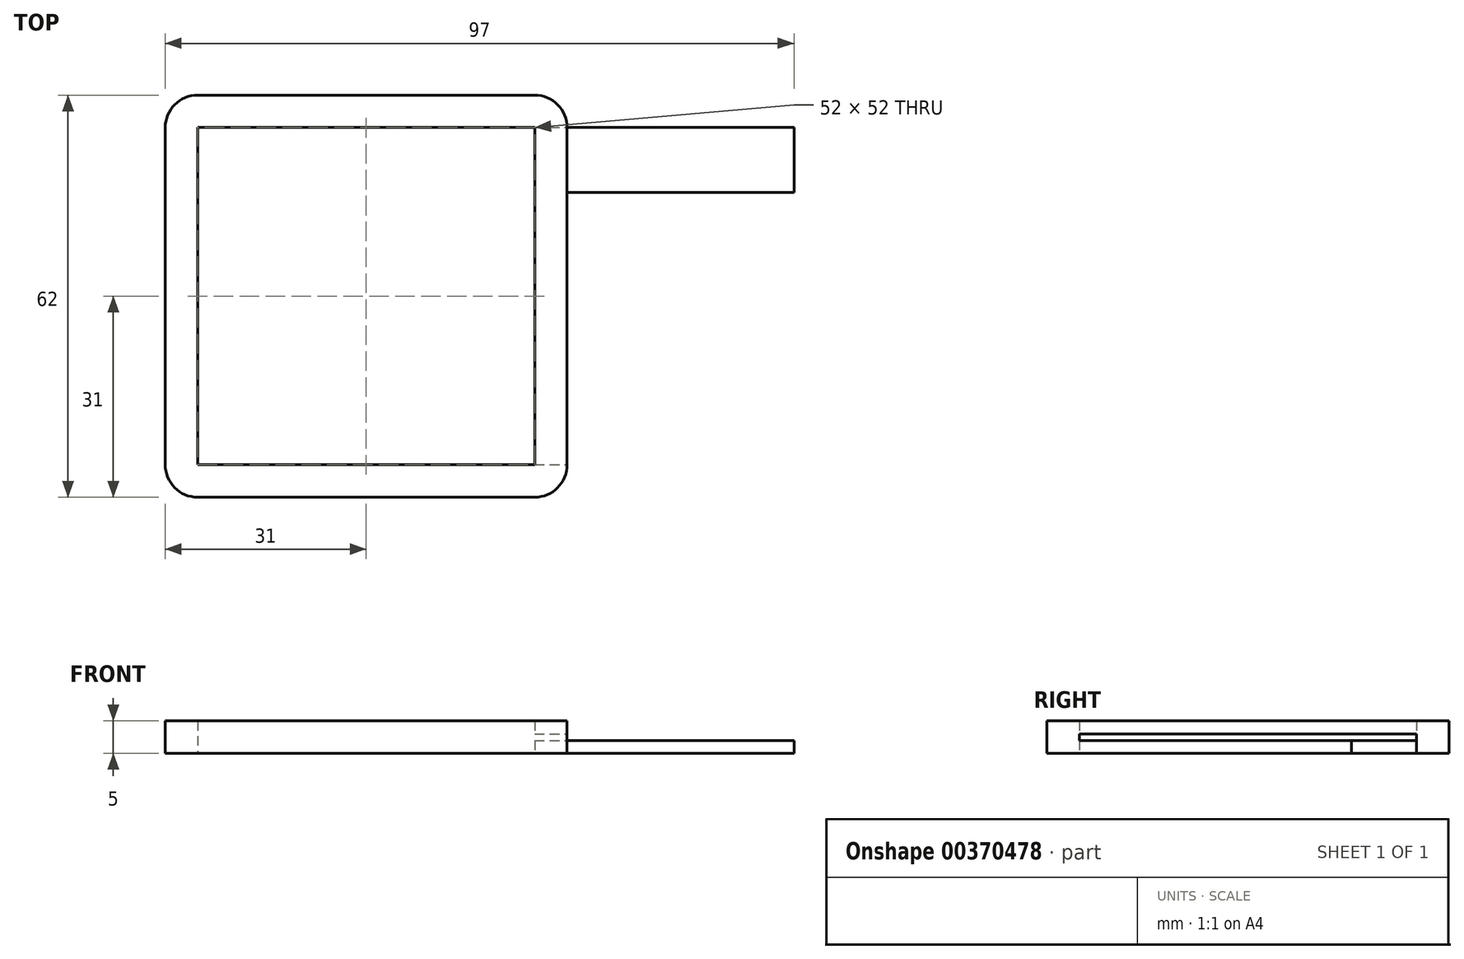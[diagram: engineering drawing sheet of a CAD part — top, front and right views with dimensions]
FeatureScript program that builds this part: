
annotation { "Feature Type Name" : "Feature", "Feature Type Description" : "" }
export const myFeature = defineFeature(function(context is Context, id is Id, definition is map)
    precondition{}
    {
        {
            var Q0;
            Q0=qCreatedBy(makeId("Top.planeOp"),FACE);
            var sketch = newSketch(context, id + "F0", { "sketchPlane" : qUnion([Q0])});
            skLineSegment(sketch, "E0.bottom", {"start": v(5, 0) * mm, "end": v(57, 0) * mm});
            skLineSegment(sketch, "E0.top", {"start": v(5, -62) * mm, "end": v(57, -62) * mm});
            skLineSegment(sketch, "E0.left", {"start": v(0, -5) * mm, "end": v(0, -57) * mm});
            skLineSegment(sketch, "E0.right", {"start": v(62, -5) * mm, "end": v(62, -57) * mm});
            skPoint(sketch, "E1.visualSharp", {"position": v(0, 0) * mm});
            skArc(sketch, "E1.filletArc", {"start": v(5, 0) * mm, "mid": v(1.46, -1.46) * mm, "end": v(0, -5) * mm});
            skPoint(sketch, "E2.visualSharp", {"position": v(0, -62) * mm});
            skArc(sketch, "E2.filletArc", {"start": v(0, -57) * mm, "mid": v(1.46, -60.54) * mm, "end": v(5, -62) * mm});
            skPoint(sketch, "E3.visualSharp", {"position": v(62, -62) * mm});
            skArc(sketch, "E3.filletArc", {"start": v(57, -62) * mm, "mid": v(60.54, -60.54) * mm, "end": v(62, -57) * mm});
            skPoint(sketch, "E4.visualSharp", {"position": v(62, 0) * mm});
            skArc(sketch, "E4.filletArc", {"start": v(62, -5) * mm, "mid": v(60.54, -1.46) * mm, "end": v(57, 0) * mm});
            skLineSegment(sketch, "E5.bottom", {"start": v(57, -5) * mm, "end": v(5, -5) * mm});
            skLineSegment(sketch, "E5.top", {"start": v(57, -57) * mm, "end": v(5, -57) * mm});
            skLineSegment(sketch, "E5.left", {"start": v(57, -5) * mm, "end": v(57, -57) * mm});
            skLineSegment(sketch, "E5.right", {"start": v(5, -5) * mm, "end": v(5, -57) * mm});
            skLineSegment(sketch, "E6.bottom", {"start": v(62, -5) * mm, "end": v(97, -5) * mm});
            skLineSegment(sketch, "E6.top", {"start": v(62, -15) * mm, "end": v(97, -15) * mm});
            skLineSegment(sketch, "E6.left", {"start": v(62, -5) * mm, "end": v(62, -15) * mm});
            skLineSegment(sketch, "E6.right", {"start": v(97, -5) * mm, "end": v(97, -15) * mm});
            skSolve(sketch);
        }
        {
            var Q0;
            Q0=makeQuery(id+"F0.imprint","IMPRINT",FACE,{"disambiguationData":[TD([[makeQuery(id+"F0.imprint","IMPRINT",EDGE,{"derivedFrom":sQuery(id+"F0.wireOp",EDGE,"E0.bottom")}),-1.0]])]});
            extrude(context, id + "F1", {"entities" : qUnion([Q0]), "depth" : 5 * mm});
        }
        {
            var Q0;
            Q0=makeQuery(id+"F0.imprint","IMPRINT",FACE,{"disambiguationData":[TD([[makeQuery(id+"F0.imprint","IMPRINT",EDGE,{"derivedFrom":sQuery(id+"F0.wireOp",EDGE,"E6.bottom")}),-1.0]])]});
            extrude(context, id + "F2", {"entities" : qUnion([Q0]), "operationType" : NewBodyOperationType.ADD, "depth" : 2 * mm});
        }
        {
            var Q0;
            Q0=makeQuery(id+"F1.opExtrude","SWEPT_FACE",FACE,{"disambiguationData":[OSD([sQuery(id+"F0.wireOp",EDGE,"E0.right"),sQuery(id+"F0.wireOp",EDGE,"E6.left")])]});
            var sketch = newSketch(context, id + "F3", { "sketchPlane" : qUnion([Q0])});
            skLineSegment(sketch, "E7.bottom", {"start": v(-5, 2) * mm, "end": v(-57, 2) * mm});
            skLineSegment(sketch, "E7.top", {"start": v(-5, 3) * mm, "end": v(-57, 3) * mm});
            skLineSegment(sketch, "E7.left", {"start": v(-5, 2) * mm, "end": v(-5, 3) * mm});
            skLineSegment(sketch, "E7.right", {"start": v(-57, 2) * mm, "end": v(-57, 3) * mm});
            skSolve(sketch);
        }
        {
            var Q0;
            Q0=makeQuery(id+"F3.imprint","IMPRINT",FACE,{"disambiguationData":[TD([[makeQuery(id+"F3.imprint","IMPRINT",EDGE,{"derivedFrom":sQuery(id+"F3.wireOp",EDGE,"E7.top")}),1.0]])]});
            extrude(context, id + "F4", {"entities" : qUnion([Q0]), "operationType" : NewBodyOperationType.REMOVE, "endBound" : BoundingType.UP_TO_NEXT, "oppositeDirection" : true, "depth" : 25 * mm});
        }
    });
